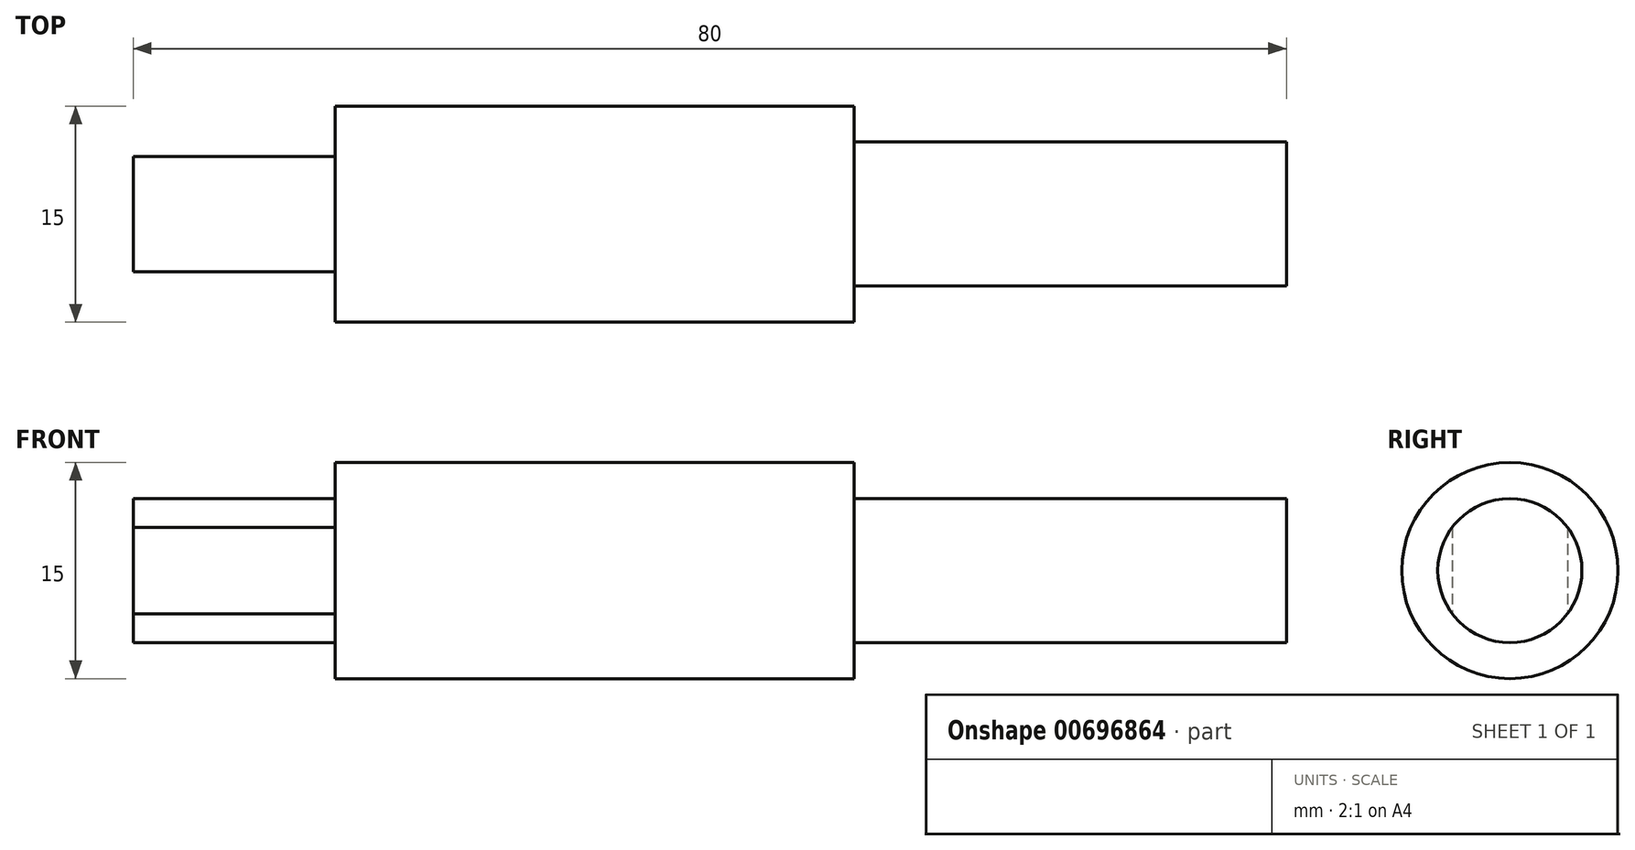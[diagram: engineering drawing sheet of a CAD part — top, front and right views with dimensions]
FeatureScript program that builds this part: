
annotation { "Feature Type Name" : "Feature", "Feature Type Description" : "" }
export const myFeature = defineFeature(function(context is Context, id is Id, definition is map)
    precondition{}
    {
        {
            var Q0;
            Q0=qCreatedBy(makeId("Right.planeOp"),FACE);
            var sketch = newSketch(context, id + "F0", { "sketchPlane" : qUnion([Q0])});
            skCircle(sketch, "E0", {"center": v(0, 0) * mm, "radius": 5 * mm});
            skSolve(sketch);
        }
        {
            var Q0;
            Q0 = qSketchRegion(id + "F0", true);
            extrude(context, id + "F1", {"entities" : qUnion([Q0]), "depth" : 80 * mm, "offsetDistance" : 25 * mm});
        }
        {
            var Q0;
            Q0=qCreatedBy(makeId("Right.planeOp"),FACE);
            cPlane(context, id + "F2", {"entities" : qUnion([Q0]), "cplaneType" : CPlaneType.OFFSET, "offset" : 14 * mm, "width" : 150 * mm, "height" : 150 * mm});
        }
        {
            var Q0;
            Q0=qCreatedBy(id+"F2.planeOp",FACE);
            var sketch = newSketch(context, id + "F3", { "sketchPlane" : qUnion([Q0])});
            skCircle(sketch, "E1", {"center": v(0, 0) * mm, "radius": 7.5 * mm});
            skSolve(sketch);
        }
        {
            var Q0;
            Q0 = qSketchRegion(id + "F3", true);
            extrude(context, id + "F4", {"entities" : qUnion([Q0]), "operationType" : NewBodyOperationType.ADD, "depth" : (80 - 30 - 14) * mm, "offsetDistance" : 25 * mm});
        }
        {
            var Q0;
            Q0=makeQuery(id+"F1.opExtrude","CAP_FACE",FACE,{"disambiguationData":[OSD([sQuery(id+"F0.wireOp",EDGE,"E0")])],"isStart":true});
            var sketch = newSketch(context, id + "F5", { "sketchPlane" : qUnion([Q0])});
            skArc(sketch, "E2.0", {"start": v(-4, 3) * mm, "mid": v(-5, 0) * mm, "end": v(-4, -3) * mm});
            skLineSegment(sketch, "E3", {"start": v(-4, 3) * mm, "end": v(-4, -3) * mm});
            skLineSegment(sketch, "E4", {"start": v(4, 3) * mm, "end": v(4, -3) * mm});
            skArc(sketch, "E5.trimOffspring", {"start": v(4, -3) * mm, "mid": v(5, 0) * mm, "end": v(4, 3) * mm});
            skSolve(sketch);
        }
        {
            var Q0;
            Q0 = qSketchRegion(id + "F5", true);
            var Q1;
            Q1=makeQuery(id+"F4.opExtrude","CAP_FACE",FACE,{"disambiguationData":[OSD([sQuery(id+"F3.wireOp",EDGE,"E1")])],"isStart":true});
            extrude(context, id + "F6", {"entities" : qUnion([Q0]), "operationType" : NewBodyOperationType.REMOVE, "endBound" : BoundingType.UP_TO_SURFACE, "oppositeDirection" : true, "depth" : 25 * mm, "endBoundEntityFace" : qUnion([Q1]), "offsetDistance" : 25 * mm});
        }
    });
